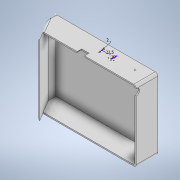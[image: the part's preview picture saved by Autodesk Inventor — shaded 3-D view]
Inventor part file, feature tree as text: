
AUTODESK INVENTOR PART (.ipt)
format: ipt  version: 2021 (Build 250183000, 183)  size: 252,928 bytes
history: native  units: mm
features: sketch x9, extrude x8, chamfer x3, fillet x3, shell x1, hole x1
ambient origin geometry x8: Origin, YZ Plane, XZ Plane, XY Plane, X Axis, Y Axis, Z Axis, Center Point
bodies: Volumenkörper1 (feature_tree)
feature tree (25):
  extrude  "Extrusion1"  Depth=132.329mm
  chamfer  "Fase1"  Distance=55.0mm
  shell  "Wandung1"  Thickness=2.5mm
  extrude  "Extrusion2"  Depth=1.0mm TaperAngle=0.0deg
  extrude  "Extrusion3"  Depth=2.5mm
  extrude  "Extrusion4"  Depth=8.0mm
  extrude  "Extrusion6"  Depth=8.0mm
  fillet  "Rundung1"  Radius=4.0mm
  fillet  "Rundung2"  Radius=4.75mm
  extrude  "Extrusion7"  Depth=10.0mm
  extrude  "Extrusion8"  Depth=10.0mm
  hole  "Bohrung3"  [1 undecoded]
  extrude  "Extrusion9"  Depth=2.0mm
  chamfer  "Fase2"  Distance=22.0mm
  chamfer  "Fase3"  Distance=13.8mm
  fillet  "Rundung3"  Radius=8.5mm
  sketch  "Skizze1"  dims[d0=190.176mm d1=132.329mm d2=55.0mm d3=0.0mm]
  sketch  "Skizze2"  dims[d4=38.0mm d5=2.0mm d6=30.0deg d7=2.5mm]
  sketch  "Skizze4"  dims[d8=15.0mm d9=0.0mm d17=1.0mm d18=0.0mm]
  sketch  "Skizze5"  dims[d19=0.0mm d20=0.0mm d22=2.5mm]
  sketch  "Skizze7"  dims[d28=6.0mm d29=8.0mm]
  sketch  "Skizze9"  dims[d30=8.0mm d31=8.0mm d32=4.0mm d33=0.0mm d34=4.75mm]
  sketch  "Skizze10"  dims[d35=4.75mm d43=1.0mm d44=10.0mm d45=22.5mm]
  sketch  "Skizze11"  dims[d46=10.0mm d47=0.0mm d48=12.0mm]
  sketch  "Skizze12"  dims[d49=10.0mm d50=0.0mm d51=3.5mm d52=2.0mm d53=2.0mm d54=6.0mm d55=4.0mm d56=2.0mm d57=90.0deg d58=5.0mm d59=0.0mm d60=22.0mm d61=13.8mm d62=8.5mm d63=10.0mm d64=0.0mm d65=2.0mm d66=2.0mm d67=30.0deg d68=2.0mm d69=2.0mm d70=30.0deg d71=80.0mm d72=2.0mm]
note: 1 required parameter value undecoded (feature->parameter linkage not recoverable at this tier; creation-order binding heuristic only, values carry confidence <= 0.55)
